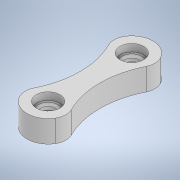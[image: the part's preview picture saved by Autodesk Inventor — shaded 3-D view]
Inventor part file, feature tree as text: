
AUTODESK INVENTOR PART (.ipt)
format: ipt  version: 2021 (Build 250183000, 183)  size: 161,280 bytes
history: native  units: mm
features: extrude x3, sketch x3, plane x1, chamfer x1, fillet x1
ambient origin geometry x8: Origin, YZ Plane, XZ Plane, XY Plane, X Axis, Y Axis, Z Axis, Center Point
bodies: Solid1 (feature_tree)
feature tree (9):
  extrude  "Extrusion1"  Depth=22.4mm
  plane  "Work Plane1"
  extrude  "Extrusion2"  Depth=79.5mm
  chamfer  "Chamfer1"  Distance=40.0mm
  extrude  "Extrusion3"  Depth=21.0mm TaperAngle=0.0deg
  fillet  "Fillet1"  [1 undecoded]
  sketch  "Sketch1"  dims[d0=22.4mm d1=22.4mm]
  sketch  "Sketch2"  dims[d2=0.0mm d3=79.5mm]
  sketch  "Sketch3"  dims[d4=40.0mm d5=40.0mm d6=21.0mm d7=0.0mm d8=-7.0mm d9=14.0mm d10=14.0mm d11=7.0mm d12=0.0mm d13=2.0mm d14=2.0mm d15=45.0deg d16=80.0mm d17=80.0mm d18=80.0mm d19=0.0mm d20=15.0mm]
note: 1 required parameter value undecoded (feature->parameter linkage not recoverable at this tier; creation-order binding heuristic only, values carry confidence <= 0.55)
